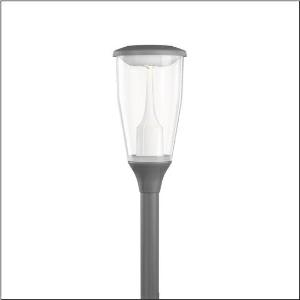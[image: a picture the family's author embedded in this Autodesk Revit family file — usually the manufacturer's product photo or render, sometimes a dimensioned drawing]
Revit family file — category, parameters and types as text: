
# Revit family: dl_11_iq___st1_2a_5xa5575ef14hp00022_53ae
name_source: partatom
category: Lighting Fixtures
units: mm (PartAtom-declared; Revit-internal decimal feet)

## family parameters
Cut with Voids When Loaded = No
Host = Face
Light Source = No
Part Type = Normal
Room Calculation Point = No
Round Connector Dimension = Use Diameter
Shared = No

## types (1)
- --- (1 x LED, 4840 lm, 33.6 W, 3000K)
    Apparent Load = 34 VA
    CIE Flux Codes = 33 63 91 94 100
    Color Rendering = 70
    Color Temperature = 3000K
    Default Elevation = 1800 mm
    Description = DL 11 iQ, mast luminaire, Module 540 iQ-SR, primary light control with 3 zone facetted reflector, of plastic, silver coated, highly specular, structured, primary optical cover: cover, of PMMA, transparent, light distribution: ST1.2a, light emission: direct distribution, primary light characteristic: asymmetric, installation type: post-top, LED, High Power LED, light colour: 730, colour temperature: 3000K, control: Street-Remote, Auto-Match, Temp-Guard, Lumen-Switch, Night-Set, Smart-Wire, Light-Fading, Desk-Remote (wireless, voltage-free reading and setting of iQ features in the workshop via application-optimized NFC function/RFID function), optimised constant luminous flux control (CLO 2.0), mains connection: 220..240V, AC, 50/60Hz, connection cable pre-assembled, cable length: 5,5m, luminaire housing, upper part, of diecast aluminium, coated, Siteco® metallic grey (DB 702S), spigot size: 76mm (post-top), post-top mast mounting element, of diecast aluminium, coated, Siteco® metallic grey (DB 702S), Module 540 iQ-SR, traffic white (RAL 9016), equipment: Power, protection rating (complete): IP66, insulation class (complete): insulation class II (safety insulation), certification: CE, ENEC, ENEC+, VDE, packaging unit: 1 piece

Light Distribution: ST1.2a
    Height = 665 mm
    Lamp = 1 x LED
    Lamp Light Flux = 4840 lm
    Lamp Power = 33.6 W
    Lamp count = 1
    Length = 334 mm
    Luminous efficacy = 144 lm/W
    Manufacturer = Siteco
    ModVariant = No
    Model = 5XA5575EF14HP00022
    Number of Poles = 1
    OnlyDefault = Yes
    Power Factor = 1
    Product Name = DL 11 iQ | ST1.2a
    Product group = mast luminaire | pylon top
    ProductGroupID = 6100
    Protection Class = Protection class II
    Protection Degree = IP 66
    RLX_Detail_Level = 1
    RLX_Emergency_Light_Flux = 0 lm
    RLX_Emergency_Type = 0
    RLX_Emergency_Type_DB = No
    RlxData = <blob elided: 98145 chars, md5=fd0ed2af>
    Socket = socket
    Standby Power = 0 W
    System Light Flux = 4840 lm
    System Power = 34 W
    Type Comments = factory setting: luminous flux: 100 % | dim-lin: 254 | 695 mA
    Type Image = l_1258354.jpg
    URL = http://relux.com
    VarID = @adj_002537
    Voltage = 0 V
    Weight = 0.00 kg
    Width = 0 mm  [stored 0 ft]

note: [stored X ft] marks values corroborated as IEEE doubles in the binary element streams (Revit-internal decimal feet)

## geometry (parser evidence)
native form markers: Blend x4, Sweep x11
no freeform markers — native parametric forms only
